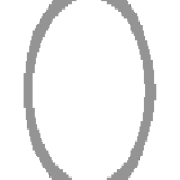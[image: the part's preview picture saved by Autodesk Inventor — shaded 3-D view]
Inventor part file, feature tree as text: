
AUTODESK INVENTOR PART (.ipt)
format: ipt  version: 2021 (Build 250183000, 183)  size: 109,056 bytes
history: native  units: in
note: dims shown in document units (in); Inventor stores cm internally (conversion verified against a paired STEP export)
features: other x4, sketch x3, plane x1
ambient origin geometry x8: Origin, YZ Plane, XZ Plane, XY Plane, X Axis, Y Axis, Z Axis, Center Point
bodies: Solid1 (feature_tree), Body (feature_tree)
feature tree (8):
  other  "Driven Length"
  other  "Frame Generator"
  other  "Start Plane"
  other  "End Plane"
  sketch  "Sketch"  dims[d2=21.1542in d4=-0.0in d5=21.1542in d6=0.12in d7=0.0in d8=90.0deg d9=21.1542in]
  sketch  "Sketch2"  dims[d0=1.0in]
  plane  "Work Plane3"
  sketch  "Sketch3"  dims[d1=0.065in]
